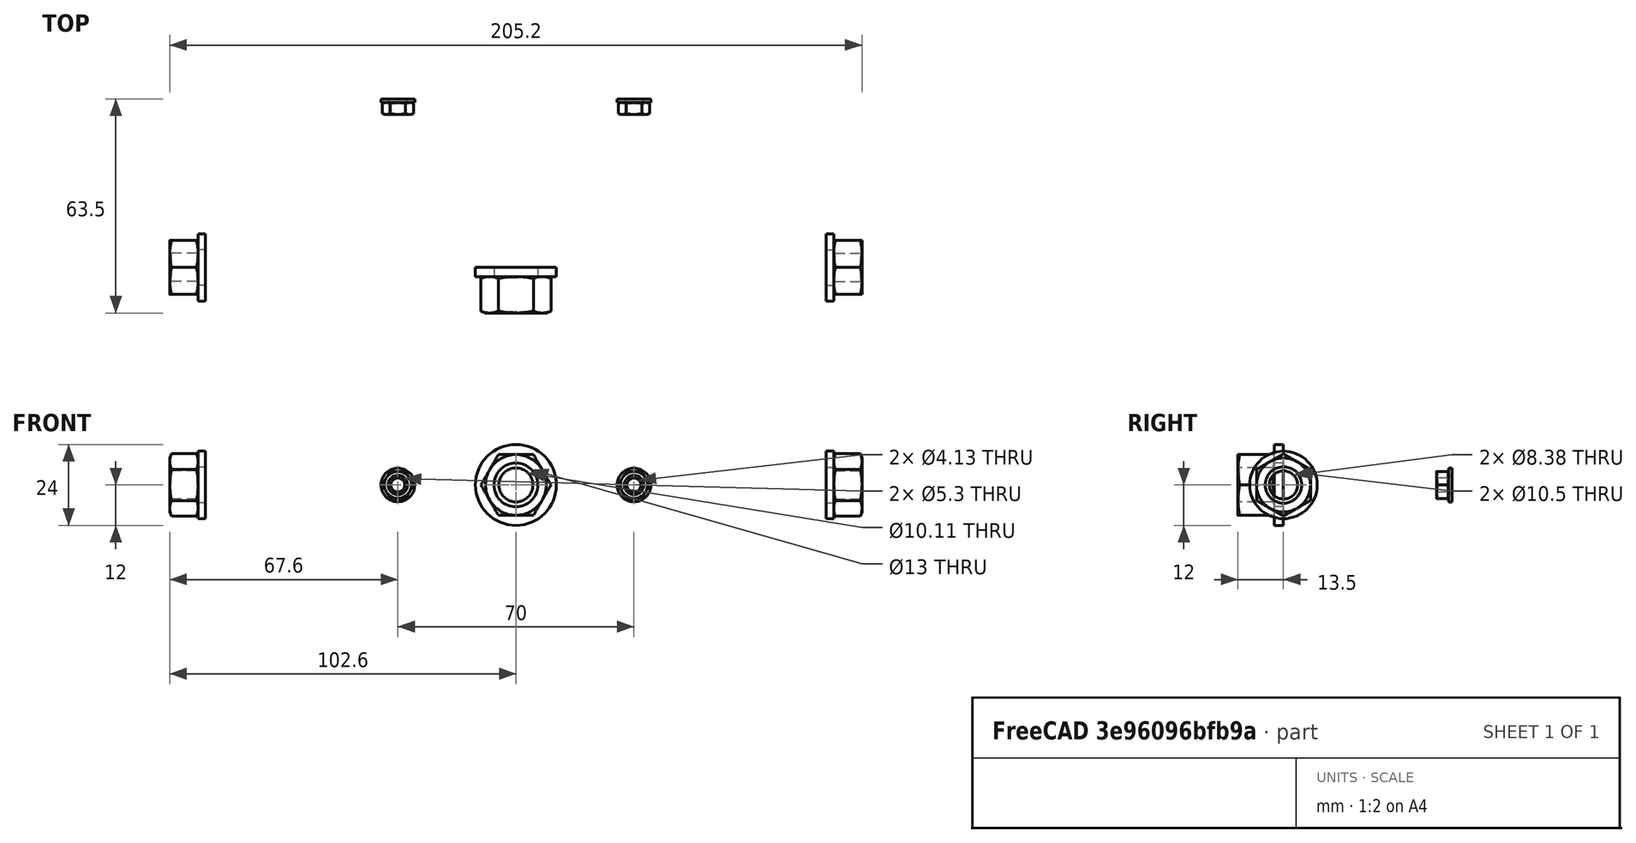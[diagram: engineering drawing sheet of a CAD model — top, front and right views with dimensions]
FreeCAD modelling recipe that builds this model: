
FCSTD DOCUMENT  (FreeCAD 0.19R)
Label: turnable_motor
License: All rights reserved
LicenseURL: http://en.wikipedia.org/wiki/All_rights_reserved
objects: Part::FeaturePython×10, PartDesign::CoordinateSystem×6, App::Link×6, App::DocumentObjectGroup×2, App::FeaturePython×1, App::Part×1
note: 16 computed .brp shape members not serialized (recipe doc carries the construction recipe); baked Part::Feature solids carry a one-line shape summary decoded from their .brp
EXTERNAL_REF file=frame.FCStd obj=LCS_1
EXTERNAL_REF file=frame.FCStd obj=Body
EXTERNAL_REF file=frame.FCStd obj=LCS_hole1
EXTERNAL_REF file=motor.FCStd obj=LCS_f1
EXTERNAL_REF file=motor.FCStd obj=Body
EXTERNAL_REF file=adapter.FCStd obj=LCS_1
EXTERNAL_REF file=motor.FCStd obj=shaft
EXTERNAL_REF file=adapter.FCStd obj=Body
EXTERNAL_REF file=adapter.FCStd obj=LCS_shaft_bottom
EXTERNAL_REF file=faceplate.FCStd obj=LCS_hole
EXTERNAL_REF file=faceplate.FCStd obj=Body
EXTERNAL_REF file=frame.FCStd obj=LCS_front1
EXTERNAL_REF file=frame.FCStd obj=LCS_front2
EXTERNAL_REF file=frame.FCStd obj=LCS_axis
EXTERNAL_REF file=stand.FCStd obj=LCS_hole
EXTERNAL_REF file=stand.FCStd obj=Body
EXTERNAL_REF file=stand.FCStd obj=LCS_sh2
EXTERNAL_REF file=stand.FCStd obj=LCS_sh1
EXTERNAL_REF file=disc.FCStd obj=LCS_back
EXTERNAL_REF file=faceplate.FCStd obj=LCS_front
EXTERNAL_REF file=disc.FCStd obj=Body
EXTERNAL_REF file=disc.FCStd obj=LCS_disc_front

FEATURE [App::DocumentObjectGroup] Parts
FEATURE [PartDesign::CoordinateSystem] LCS_Origin
  AttacherType = Attacher::AttachEngine3D
  MapMode = 2
  Support = -> [X_Axis]
FEATURE [App::DocumentObjectGroup] Constraints
FEATURE [App::FeaturePython] Variables  # WARN: FeaturePython — macro-defined, semantics opaque (R4)
FEATURE [App::Link] frame_Body
  AssemblyType = Asm4EE
  AttachedBy = #LCS_1
  AttachedTo = Parent Assembly#LCS_Origin
  AttachmentOffset = pos=(0,0,0) rot=(0.57735,0.57735,0.57735;2.0944rad)
  LinkPlacement = pos=(-56,1.51e-14,8e-15) rot=(0,0,1;0rad)
  LinkedObject = -> <external frame.FCStd>#Body
  Placement = pos=(-56,1.51e-14,8e-15) rot=(0,0,1;0rad)
  expr: Placement = LCS_Origin.Placement * AttachmentOffset * frame#LCS_1.Placement ^ -1
FEATURE [App::Link] motor_Body
  AssemblyType = Asm4EE
  AttachedBy = #LCS_f1
  AttachedTo = frame_Body#LCS_hole1
  LinkPlacement = pos=(-56,94,56) rot=(0,0,1;0rad)
  LinkedObject = -> <external motor.FCStd>#Body
  Placement = pos=(-56,94,56) rot=(0,0,1;0rad)
  expr: Placement = frame_Body.Placement * frame#LCS_hole1.Placement * AttachmentOffset * motor#LCS_f1.Placement ^ -1
FEATURE [App::Link] adapter_Body
  AssemblyType = Asm4EE
  AttachedBy = #LCS_1
  AttachedTo = motor_Body#shaft
  AttachmentOffset = pos=(0,0,0) rot=(1,0,0;3.14159rad)
  LinkPlacement = pos=(-56,-6,56) rot=(0,1,0;3.14159rad)
  LinkedObject = -> <external adapter.FCStd>#Body
  Placement = pos=(-56,-6,56) rot=(0,1,0;3.14159rad)
  expr: Placement = motor_Body.Placement * motor#shaft.Placement * AttachmentOffset * adapter#LCS_1.Placement ^ -1
FEATURE [App::Link] faceplate_Body
  AssemblyType = Asm4EE
  AttachedBy = #LCS_hole
  AttachedTo = adapter_Body#LCS_shaft_bottom
  AttachmentOffset = pos=(0,0,0) rot=(1,0,0;3.14159rad)
  LinkPlacement = pos=(-56,-39,56) rot=(0,0,1;0rad)
  LinkedObject = -> <external faceplate.FCStd>#Body
  Placement = pos=(-56,-39,56) rot=(0,0,1;0rad)
  expr: Placement = adapter_Body.Placement * adapter#LCS_shaft_bottom.Placement * AttachmentOffset * faceplate#LCS_hole.Placement ^ -1
FEATURE [Part::FeaturePython] Washer001  label="M5-Washer"  # Fasteners workbench fastener (typed FeaturePython)
  AssemblyType = Asm4EE
  AttachedBy = Origin
  AttachedTo = frame_Body#LCS_front1
  Placement = pos=(-91,3.92e-14,56) rot=(0.57735,-0.57735,0.57735;2.0944rad)
  diameter = 6
  invert = false
  matchOuter = false
  offset = 0
  type = 3
  expr: Placement = frame_Body.Placement * frame#LCS_front1.Placement * AttachmentOffset
FEATURE [Part::FeaturePython] Washer002  label="M5-Washer001"  # Fasteners workbench fastener (typed FeaturePython)
  AssemblyType = Asm4EE
  AttachedBy = Origin
  AttachedTo = frame_Body#LCS_front2
  Placement = pos=(-21,1.59e-14,56) rot=(0.57735,-0.57735,0.57735;2.0944rad)
  diameter = 6
  invert = false
  matchOuter = false
  offset = 0
  type = 3
  expr: Placement = frame_Body.Placement * frame#LCS_front2.Placement * AttachmentOffset
FEATURE [PartDesign::CoordinateSystem] LCS_w1
  AttacherType = Attacher::AttachEngine3D
  MapMode = 11
  Placement = pos=(-21,-1.1,56) rot=(0,-0.707107,0.707107;3.14159rad)
  Support = -> [Washer002]
FEATURE [PartDesign::CoordinateSystem] LCS_w2
  AttacherType = Attacher::AttachEngine3D
  MapMode = 11
  Placement = pos=(-91,-1.1,56) rot=(0,-0.707107,0.707107;3.14159rad)
  Support = -> [Washer001]
FEATURE [Part::FeaturePython] Nut001  label="M5-Nut"  # Fasteners workbench fastener (typed FeaturePython)
  AssemblyType = Asm4EE
  AttachedBy = Origin
  AttachedTo = Parent Assembly#LCS_w1
  Placement = pos=(-21,-1.1,56) rot=(0,-0.707107,0.707107;3.14159rad)
  diameter = 7
  invert = false
  matchOuter = false
  offset = 0
  thread = false
  type = 7
  expr: Placement = LCS_w1.Placement * AttachmentOffset
FEATURE [Part::FeaturePython] Nut002  label="M5-Nut001"  # Fasteners workbench fastener (typed FeaturePython)
  AssemblyType = Asm4EE
  AttachedBy = Origin
  AttachedTo = Parent Assembly#LCS_w2
  Placement = pos=(-91,-1.1,56) rot=(0,-0.707107,0.707107;3.14159rad)
  diameter = 7
  invert = false
  matchOuter = false
  offset = 0
  thread = false
  type = 7
  expr: Placement = LCS_w2.Placement * AttachmentOffset
FEATURE [App::Link] stand_Body
  AssemblyType = Asm4EE
  AttachedBy = #LCS_hole
  AttachedTo = frame_Body#LCS_axis
  AttachmentOffset = pos=(0,0,0) rot=(0.707107,-0.707107,0;3.14159rad)
  LinkPlacement = pos=(-56,-250,-180) rot=(0,0,-1;3.14159rad)
  LinkedObject = -> <external stand.FCStd>#Body
  Placement = pos=(-56,-250,-180) rot=(0,0,-1;3.14159rad)
  expr: Placement = frame_Body.Placement * frame#LCS_axis.Placement * AttachmentOffset * stand#LCS_hole.Placement ^ -1
FEATURE [Part::FeaturePython] Washer003  label="M10-Washer"  # Fasteners workbench fastener (typed FeaturePython)
  AssemblyType = Asm4EE
  AttachedBy = Origin
  AttachedTo = stand_Body#LCS_sh2
  AttachmentOffset = pos=(0,0,0) rot=(1,0,0;3.14159rad)
  Placement = pos=(36,-50,56) rot=(0.57735,0.57735,0.57735;2.0944rad)
  diameter = 9
  invert = false
  matchOuter = false
  offset = 0
  type = 3
  expr: Placement = stand_Body.Placement * stand#LCS_sh2.Placement * AttachmentOffset
FEATURE [PartDesign::CoordinateSystem] LCS_sw1
  AttacherType = Attacher::AttachEngine3D
  MapMode = 11
  Placement = pos=(38.2,-50,56) rot=(0.707107,0,0.707107;3.14159rad)
  Support = -> [Washer003]
FEATURE [Part::FeaturePython] Nut003  label="M10-Nut"  # Fasteners workbench fastener (typed FeaturePython)
  AssemblyType = Asm4EE
  AttachedBy = Origin
  AttachedTo = Parent Assembly#LCS_sw1
  Placement = pos=(38.2,-50,56) rot=(0.707107,0,0.707107;3.14159rad)
  diameter = 10
  invert = false
  matchOuter = false
  offset = 0
  thread = false
  type = 7
  expr: Placement = LCS_sw1.Placement * AttachmentOffset
FEATURE [Part::FeaturePython] Washer004  label="M10-Washer001"  # Fasteners workbench fastener (typed FeaturePython)
  AssemblyType = Asm4EE
  AttachedBy = Origin
  AttachedTo = stand_Body#LCS_sh1
  Placement = pos=(-148,-50,56) rot=(-0.57735,-0.57735,0.57735;2.0944rad)
  diameter = 9
  invert = false
  matchOuter = false
  offset = 0
  type = 3
  expr: Placement = stand_Body.Placement * stand#LCS_sh1.Placement * AttachmentOffset
FEATURE [PartDesign::CoordinateSystem] LCS_sw2
  AttacherType = Attacher::AttachEngine3D
  MapMode = 11
  Placement = pos=(-150.2,-50,56) rot=(-0.707107,0,0.707107;3.14159rad)
  Support = -> [Washer004]
FEATURE [Part::FeaturePython] Nut005  label="M10-Nut001"  # Fasteners workbench fastener (typed FeaturePython)
  AssemblyType = Asm4EE
  AttachedBy = Origin
  AttachedTo = Parent Assembly#LCS_sw2
  Placement = pos=(-150.2,-50,56) rot=(-0.707107,0,0.707107;3.14159rad)
  diameter = 10
  invert = false
  matchOuter = false
  offset = 0
  thread = false
  type = 7
  expr: Placement = LCS_sw2.Placement * AttachmentOffset
FEATURE [App::Link] disc_Body
  AssemblyType = Asm4EE
  AttachedBy = #LCS_back
  AttachedTo = faceplate_Body#LCS_front
  AttachmentOffset = pos=(0,0,0) rot=(1,0,0;3.14159rad)
  LinkPlacement = pos=(-56,-49,56) rot=(0,1,0;3.14159rad)
  LinkedObject = -> <external disc.FCStd>#Body
  Placement = pos=(-56,-49,56) rot=(0,1,0;3.14159rad)
  expr: Placement = faceplate_Body.Placement * faceplate#LCS_front.Placement * AttachmentOffset * disc#LCS_back.Placement ^ -1
FEATURE [Part::FeaturePython] Washer  label="M12-Washer"  # Fasteners workbench fastener (typed FeaturePython)
  AssemblyType = Asm4EE
  AttachedBy = Origin
  AttachedTo = disc_Body#LCS_disc_front
  Placement = pos=(-56,-50,56) rot=(0.57735,0.57735,-0.57735;2.0944rad)
  diameter = 10
  invert = false
  matchOuter = false
  offset = 0
  type = 3
  expr: Placement = disc_Body.Placement * disc#LCS_disc_front.Placement * AttachmentOffset
FEATURE [PartDesign::CoordinateSystem] LCS_1
  AttacherType = Attacher::AttachEngine3D
  MapMode = 11
  Placement = pos=(-56,-52.7,56) rot=(1,0,0;1.5708rad)
  Support = -> [Washer]
FEATURE [Part::FeaturePython] Nut  label="M12-Nut"  # Fasteners workbench fastener (typed FeaturePython)
  AssemblyType = Asm4EE
  AttachedBy = Origin
  AttachedTo = Parent Assembly#LCS_1
  Placement = pos=(-56,-52.7,56) rot=(1,0,0;1.5708rad)
  diameter = 11
  invert = false
  matchOuter = false
  offset = 0
  thread = false
  type = 7
  expr: Placement = LCS_1.Placement * AttachmentOffset
FEATURE [App::Part] Model
  Configuration = 0
  Group = -> [LCS_Origin,Constraints,Variables,frame_Body,motor_Body,adapter_Body,faceplate_Body,Washer001,Washer002,LCS_w1,LCS_w2,Nut001,Nut002,stand_Body,Washer003,LCS_sw1,Nut003,Washer004,LCS_sw2,Nut005,disc_Body,Washer,LCS_1,Nut]
  Origin = -> Origin
  Type = Assembly4 Model

RESOLVED EXTERNAL PARTS (link-assembly join: the EXTERNAL_REF files above that resolve inside this repo's crawl, each included once):
---- part adapter.FCStd = doc fcstd_3b703603a306 ----
FCSTD DOCUMENT  (FreeCAD 0.19R)
Label: adapter
License: All rights reserved
LicenseURL: http://en.wikipedia.org/wiki/All_rights_reserved
objects: Sketcher::SketchObject×3, PartDesign::Pad×2, PartDesign::CoordinateSystem×2, PartDesign::Pocket×1, PartDesign::Body×1
note: 12 computed .brp shape members not serialized (recipe doc carries the construction recipe); baked Part::Feature solids carry a one-line shape summary decoded from their .brp

FEATURE [Sketcher::SketchObject] Sketch
  FullyConstrained = false
  MapMode = 5
  Placement = pos=(0,0,0) rot=(1,0,0;1.5708rad)
  Support = -> [XZ_Plane]
  sketch-geometry (1):
    g0: Circle CenterX=0 CenterY=0 CenterZ=0 NormalX=0 NormalY=0 NormalZ=1 AngleXU=0 Radius=9.5
  constraints (1):
    c: Diameter(g0) = 19
FEATURE [PartDesign::Pad] Pad
  Direction = (1,1,1)
  Length = 33
  Length2 = 100
  Placement = pos=(0,0,0) rot=(1,0,0;1.5708rad)
  Profile = -> Sketch
  Type = 0
FEATURE [Sketcher::SketchObject] Sketch001
  FullyConstrained = true
  MapMode = 5
  Placement = pos=(0,0,0) rot=(-1,0,0;1.5708rad)
  Support = -> [Pad]
  sketch-geometry (1):
    g0: Circle CenterX=0 CenterY=0 CenterZ=0 NormalX=0 NormalY=0 NormalZ=1 AngleXU=0 Radius=4
  constraints (2):
    c: Coincident(g0,g-1)
    c: Diameter(g0) = 8
FEATURE [PartDesign::Pocket] Pocket
  BaseFeature = -> Pad
  Length = 30
  Length2 = 100
  Placement = pos=(0,0,0) rot=(1,0,0;1.5708rad)
  Profile = -> Sketch001
  Type = 0
FEATURE [Sketcher::SketchObject] Sketch002
  FullyConstrained = true
  MapMode = 5
  Placement = pos=(0,-33,7.3e-15) rot=(1,0,0;1.5708rad)
  Support = -> [Pocket]
  sketch-geometry (1):
    g0: Circle CenterX=0 CenterY=0 CenterZ=0 NormalX=0 NormalY=0 NormalZ=1 AngleXU=0 Radius=6.25
  constraints (2):
    c: Coincident(g0,g-1)
    c: Diameter(g0) = 12.5
FEATURE [PartDesign::Pad] Pad001
  BaseFeature = -> Pocket
  Direction = (1,1,1)
  Length = 23.5
  Length2 = 100
  Placement = pos=(0,0,0) rot=(1,0,0;1.5708rad)
  Profile = -> Sketch002
  Type = 0
FEATURE [PartDesign::CoordinateSystem] LCS_1
  AttacherType = Attacher::AttachEngine3D
  MapMode = 11
  Placement = pos=(0,-30,2.8e-14) rot=(0.57735,-0.57735,-0.57735;4.18879rad)
  Support = -> [Pad001]
FEATURE [PartDesign::CoordinateSystem] LCS_shaft_bottom
  AttacherType = Attacher::AttachEngine3D
  MapMode = 11
  Placement = pos=(0,-33,3.7e-14) rot=(0.57735,-0.57735,0.57735;2.0944rad)
  Support = -> [Pad001]
FEATURE [PartDesign::Body] Body
  Group = -> [Sketch,Pad,Sketch001,Pocket,Sketch002,Pad001,LCS_1,LCS_shaft_bottom]
  Origin = -> Origin
  Tip = -> Pad001
---- part disc.FCStd = doc fcstd_dda78c2396a7 ----
FCSTD DOCUMENT  (FreeCAD 0.19R)
Label: disc
License: All rights reserved
LicenseURL: http://en.wikipedia.org/wiki/All_rights_reserved
objects: TechDraw::DrawViewDimension×4, TechDraw::DrawViewPart×3, PartDesign::CoordinateSystem×2, Sketcher::SketchObject×1, PartDesign::Pad×1, PartDesign::Body×1, TechDraw::DrawSVGTemplate×1, TechDraw::DrawPage×1
note: 6 computed .brp shape members not serialized (recipe doc carries the construction recipe); baked Part::Feature solids carry a one-line shape summary decoded from their .brp

FEATURE [Sketcher::SketchObject] Sketch
  FullyConstrained = true
  MapMode = 5
  Placement = pos=(0,0,0) rot=(1,0,0;1.5708rad)
  Support = -> [XZ_Plane]
  sketch-geometry (2):
    g0: Circle CenterX=0 CenterY=0 CenterZ=0 NormalX=0 NormalY=0 NormalZ=1 AngleXU=0 Radius=77
    g1: Circle CenterX=0 CenterY=0 CenterZ=0 NormalX=0 NormalY=0 NormalZ=1 AngleXU=0 Radius=6.35
  constraints (4):
    c: Coincident(g0,g-1)
    c: Coincident(g1,g0)
    c: Diameter(g1) = 12.7
    c: Diameter(g0) = 154
FEATURE [PartDesign::Pad] Pad
  Direction = (1,1,1)
  Length = 1
  Length2 = 100
  Placement = pos=(0,0,0) rot=(1,0,0;1.5708rad)
  Profile = -> Sketch
  Type = 0
FEATURE [PartDesign::CoordinateSystem] LCS_back
  AttacherType = Attacher::AttachEngine3D
  MapMode = 11
  Placement = pos=(0,0,0) rot=(0.57735,-0.57735,0.57735;2.0944rad)
  Support = -> [Pad]
FEATURE [PartDesign::CoordinateSystem] LCS_disc_front
  AttacherType = Attacher::AttachEngine3D
  MapMode = 11
  Placement = pos=(0,-1,0) rot=(0.57735,-0.57735,0.57735;2.0944rad)
  Support = -> [Pad]
FEATURE [PartDesign::Body] Body
  Group = -> [Sketch,Pad,LCS_back,LCS_disc_front]
  Origin = -> Origin
  Tip = -> Pad
FEATURE [TechDraw::DrawSVGTemplate] Template
  EditableTexts = Designed_by_Name=Designed by Name; Drawing_number=Drawing number; FC-Date=Date; FC-SC=Scale; FC-SH=Sheet; FC-Title=Title; Subtitle=Subtitle; Weight=Weight
  Height = 210
  Orientation = 1
  Width = 297
FEATURE [TechDraw::DrawViewPart] View
  CoarseView = false
  Direction = (0,-1,0)
  Focus = 100
  HardHidden = false
  IsoCount = 0
  IsoHidden = false
  IsoVisible = false
  LockPosition = false
  Perspective = false
  Rotation = 0
  Scale = 0.3
  ScaleType = 0
  SeamHidden = false
  SeamVisible = true
  SmoothHidden = false
  SmoothVisible = true
  Source = -> [Pad]
  X = 80.5
  XDirection = (-0.494,0,-0.83)
  Y = 155
FEATURE [TechDraw::DrawViewPart] View001
  CoarseView = false
  Direction = (0.264,-0.596,0.758)
  Focus = 100
  HardHidden = false
  IsoCount = 0
  IsoHidden = false
  IsoVisible = false
  LockPosition = false
  Perspective = false
  Rotation = 0
  Scale = 0.4
  ScaleType = 0
  SeamHidden = false
  SeamVisible = true
  SmoothHidden = false
  SmoothVisible = true
  Source = -> [Body]
  X = 215.5
  XDirection = (0.492,0.759,0.426)
  Y = 152
FEATURE [TechDraw::DrawViewPart] View002
  CoarseView = false
  Direction = (0,0,1)
  Focus = 100
  HardHidden = false
  IsoCount = 0
  IsoHidden = false
  IsoVisible = false
  LockPosition = false
  Perspective = false
  Rotation = 0
  Scale = 0.7
  ScaleType = 0
  SeamHidden = false
  SeamVisible = true
  SmoothHidden = false
  SmoothVisible = true
  Source = -> [Body]
  X = 90.5
  XDirection = (1,0,0)
  Y = 87
FEATURE [TechDraw::DrawViewDimension] Dimension
  Arbitrary = false
  ArbitraryTolerances = false
  EqualTolerance = true
  FormatSpec = %.2f
  FormatSpecOverTolerance = %+.2f
  FormatSpecUnderTolerance = %+.2f
  Inverted = false
  LockPosition = false
  MeasureType = 1
  OverTolerance = 0
  References2D = -> [View002]
  Rotation = 0
  ScaleType = 0
  TheoreticalExact = false
  Type = 0
  UnderTolerance = 0
  X = 0
  Y = -0.5
FEATURE [TechDraw::DrawViewDimension] Dimension002
  Arbitrary = false
  ArbitraryTolerances = false
  EqualTolerance = true
  FormatSpec = ⌀%.2f
  FormatSpecOverTolerance = %+.2f
  FormatSpecUnderTolerance = %+.2f
  Inverted = false
  LockPosition = false
  MeasureType = 1
  OverTolerance = 0
  References2D = -> [View]
  Rotation = 0
  ScaleType = 0
  TheoreticalExact = false
  Type = 5
  UnderTolerance = 0
  X = -13
  Y = 0
FEATURE [TechDraw::DrawViewDimension] Dimension004
  Arbitrary = false
  ArbitraryTolerances = false
  EqualTolerance = true
  FormatSpec = %.2f
  FormatSpecOverTolerance = %+.2f
  FormatSpecUnderTolerance = %+.2f
  Inverted = false
  LockPosition = false
  MeasureType = 1
  OverTolerance = 0
  References2D = -> [View002]
  Rotation = 0
  ScaleType = 0
  TheoreticalExact = false
  Type = 2
  UnderTolerance = 0
  X = 61.9
  Y = 0
FEATURE [TechDraw::DrawViewDimension] Dimension005
  Arbitrary = false
  ArbitraryTolerances = false
  EqualTolerance = true
  FormatSpec = ⌀%.2f
  FormatSpecOverTolerance = %+.2f
  FormatSpecUnderTolerance = %+.2f
  Inverted = false
  LockPosition = false
  MeasureType = 1
  OverTolerance = 0
  References2D = -> [View]
  Rotation = 0
  ScaleType = 0
  TheoreticalExact = false
  Type = 5
  UnderTolerance = 0
  X = 12
  Y = 0
FEATURE [TechDraw::DrawPage] Page
  KeepUpdated = true
  NextBalloonIndex = 1
  ProjectionType = 0
  Template = -> Template
  Views = -> [View,View001,View002,Dimension,Dimension002,Dimension004,Dimension005]
---- part faceplate.FCStd = doc fcstd_74a67d757d3e ----
FCSTD DOCUMENT  (FreeCAD 0.19R)
Label: faceplate
License: All rights reserved
LicenseURL: http://en.wikipedia.org/wiki/All_rights_reserved
objects: Sketcher::SketchObject×3, PartDesign::Pocket×2, PartDesign::CoordinateSystem×2, PartDesign::Pad×1, PartDesign::Body×1
note: 12 computed .brp shape members not serialized (recipe doc carries the construction recipe); baked Part::Feature solids carry a one-line shape summary decoded from their .brp

FEATURE [Sketcher::SketchObject] Sketch
  FullyConstrained = true
  MapMode = 5
  Placement = pos=(0,0,0) rot=(1,0,0;1.5708rad)
  Support = -> [XZ_Plane]
  sketch-geometry (1):
    g0: Circle CenterX=0 CenterY=0 CenterZ=0 NormalX=0 NormalY=0 NormalZ=1 AngleXU=0 Radius=74.5
  constraints (2):
    c: Coincident(g0,g-1)
    c: Diameter(g0) = 149
FEATURE [PartDesign::Pad] Pad
  Direction = (1,1,1)
  Length = 10
  Length2 = 100
  Placement = pos=(0,0,0) rot=(1,0,0;1.5708rad)
  Profile = -> Sketch
  Type = 0
FEATURE [Sketcher::SketchObject] Sketch001
  FullyConstrained = true
  MapMode = 5
  Placement = pos=(0,0,0) rot=(-1,0,0;1.5708rad)
  Support = -> [Pad]
  sketch-geometry (1):
    g0: Circle CenterX=0 CenterY=0 CenterZ=0 NormalX=0 NormalY=0 NormalZ=1 AngleXU=0 Radius=6.35
  constraints (2):
    c: Coincident(g0,g-1)
    c: Diameter(g0) = 12.7
FEATURE [PartDesign::Pocket] Pocket
  BaseFeature = -> Pad
  Length = 5
  Length2 = 100
  Placement = pos=(0,0,0) rot=(1,0,0;1.5708rad)
  Profile = -> Sketch001
  Type = 1
FEATURE [PartDesign::CoordinateSystem] LCS_hole
  AttacherType = Attacher::AttachEngine3D
  MapMode = 11
  Placement = pos=(0,0,0) rot=(0.57735,-0.57735,-0.57735;4.18879rad)
  Support = -> [Pocket]
FEATURE [Sketcher::SketchObject] Sketch002
  FullyConstrained = true
  MapMode = 5
  Placement = pos=(0,0,0) rot=(-1,0,0;1.5708rad)
  Support = -> [Pocket]
  sketch-geometry (2):
    g0: Circle CenterX=0 CenterY=0 CenterZ=0 NormalX=0 NormalY=0 NormalZ=1 AngleXU=0 Radius=65
    g1: Circle CenterX=0 CenterY=0 CenterZ=0 NormalX=0 NormalY=0 NormalZ=1 AngleXU=0 Radius=34.5
  constraints (4):
    c: Coincident(g0,g-1)
    c: Coincident(g1,g0)
    c: Diameter(g1) = 69
    c: Diameter(g0) = 130
FEATURE [PartDesign::Pocket] Pocket001
  BaseFeature = -> Pocket
  Length = 6
  Length2 = 100
  Placement = pos=(0,0,0) rot=(1,0,0;1.5708rad)
  Profile = -> Sketch002
  Type = 0
FEATURE [PartDesign::CoordinateSystem] LCS_front
  AttacherType = Attacher::AttachEngine3D
  MapMode = 11
  Placement = pos=(0,-10,8.9e-15) rot=(0.57735,-0.57735,-0.57735;4.18879rad)
  Support = -> [Pocket001]
FEATURE [PartDesign::Body] Body
  Group = -> [Sketch,Pad,Sketch001,Pocket,LCS_hole,Sketch002,Pocket001,LCS_front]
  Origin = -> Origin
  Tip = -> Pocket001
---- part frame.FCStd = doc fcstd_d6c5ef4f96c6 ----
FCSTD DOCUMENT  (FreeCAD 0.19R)
Label: frame
License: All rights reserved
LicenseURL: http://en.wikipedia.org/wiki/All_rights_reserved
objects: Sketcher::SketchObject×10, PartDesign::Pad×6, PartDesign::CoordinateSystem×6, PartDesign::Pocket×4, PartDesign::Body×1
note: 37 computed .brp shape members not serialized (recipe doc carries the construction recipe); baked Part::Feature solids carry a one-line shape summary decoded from their .brp

FEATURE [Sketcher::SketchObject] Sketch
  FullyConstrained = true
  MapMode = 5
  Support = -> [XY_Plane]
  sketch-geometry (8):
    g0: LineSegment StartX=-56 StartY=32 StartZ=0 EndX=-56 EndY=0 EndZ=0
    g1: LineSegment StartX=56 StartY=32 StartZ=0 EndX=56 EndY=0 EndZ=0
    g2: LineSegment StartX=56 StartY=0 StartZ=0 EndX=-56 EndY=0 EndZ=0
    g3: LineSegment StartX=52 StartY=28 StartZ=0 EndX=52 EndY=4 EndZ=0
    g4: LineSegment StartX=52 StartY=4 StartZ=0 EndX=-52 EndY=4 EndZ=0
    g5: LineSegment StartX=-52 StartY=4 StartZ=0 EndX=-52 EndY=28 EndZ=0
    g6: ArcOfCircle CenterX=-56 CenterY=28 CenterZ=0 NormalX=0 NormalY=0 NormalZ=1 AngleXU=0 Radius=4 StartAngle=-3.64e-14 EndAngle=1.5708
    g7: ArcOfCircle CenterX=56 CenterY=28 CenterZ=0 NormalX=0 NormalY=0 NormalZ=1 AngleXU=0 Radius=4 StartAngle=1.5708 EndAngle=3.14159
  constraints (24):
    c: PointOnObject(g0,g-1)
    c: Vertical(g0)
    c: PointOnObject(g1,g-1)
    c: Vertical(g1)
    c: Coincident(g2,g1)
    c: Vertical(g3)
    c: Coincident(g4,g3)
    c: Horizontal(g4)
    c: Vertical(g5)
    c: DistanceX(g0,g1) = 112
    c: Symmetric(g0,g1,g-2)
    c: DistanceX(g3,g1) = 4
    c: DistanceY(g2,g4) = 4
    c: Symmetric(g5,g3,g-2)
    c: Coincident(g4,g5)
    c: Coincident(g2,g0)
    c: DistanceY(g4,g5) = 24
    c: DistanceY(g0,g0) = 32
    c: PointOnObject(g6,g0)
    c: Coincident(g6,g5)
    c: Coincident(g6,g0)
    c: PointOnObject(g7,g1)
    c: Coincident(g7,g3)
    c: Coincident(g7,g1)
FEATURE [PartDesign::Pad] Pad
  Direction = (1,1,1)
  Length = 112
  Length2 = 100
  Profile = -> Sketch
  Type = 0
FEATURE [Sketcher::SketchObject] Sketch001
  FullyConstrained = true
  MapMode = 5
  Placement = pos=(56,0,0) rot=(0.57735,0.57735,0.57735;2.0944rad)
  Support = -> [Pad]
  sketch-geometry (8):
    g0: LineSegment StartX=0 StartY=112 StartZ=0 EndX=32 EndY=112 EndZ=0
    g1: LineSegment StartX=0 StartY=108 StartZ=0 EndX=28 EndY=108 EndZ=0
    g2: LineSegment StartX=0 StartY=108 StartZ=0 EndX=0 EndY=112 EndZ=0
    g3: ArcOfCircle CenterX=28 CenterY=112 CenterZ=0 NormalX=0 NormalY=0 NormalZ=1 AngleXU=0 Radius=4 StartAngle=4.71239 EndAngle=6.28319
    g4: LineSegment StartX=0 StartY=0 StartZ=0 EndX=32 EndY=0 EndZ=0
    g5: LineSegment StartX=0 StartY=0 StartZ=0 EndX=0 EndY=4 EndZ=0
    g6: LineSegment StartX=0 StartY=4 StartZ=0 EndX=28 EndY=4 EndZ=0
    g7: ArcOfCircle CenterX=28 CenterY=0 CenterZ=0 NormalX=0 NormalY=0 NormalZ=1 AngleXU=0 Radius=4 StartAngle=0 EndAngle=1.5708
  constraints (25):
    c: PointOnObject(g0,g-2)
    c: Horizontal(g0)
    c: PointOnObject(g1,g-2)
    c: Horizontal(g1)
    c: Coincident(g2,g1)
    c: Coincident(g2,g0)
    c: DistanceX(g0,g0) = 32
    c: DistanceX(g1,g1) = 28
    c: DistanceY(g1,g0) = 4
    c: DistanceY(g-1,g0) = 112
    c: PointOnObject(g3,g0)
    c: Coincident(g3,g0)
    c: Coincident(g3,g1)
    c: Coincident(g4,g-1)
    c: PointOnObject(g4,g-1)
    c: DistanceX(g4,g4) = 32
    c: Coincident(g5,g4)
    c: PointOnObject(g5,g-2)
    c: Coincident(g6,g5)
    c: Horizontal(g6)
    c: DistanceY(g4,g5) = 4
    c: DistanceX(g5,g6) = 28
    c: PointOnObject(g7,g4)
    c: Coincident(g7,g6)
    c: Coincident(g7,g4)
FEATURE [PartDesign::Pad] Pad001
  BaseFeature = -> Pad
  Direction = (1,1,1)
  Length = 112
  Length2 = 100
  Profile = -> Sketch001
  Reversed = true
  Type = 0
FEATURE [Sketcher::SketchObject] Sketch002
  ExternalGeometry = -> [Pad001]
  FullyConstrained = true
  MapMode = 5
  Placement = pos=(0,0,0) rot=(1,0,0;1.5708rad)
  Support = -> [Pad001]
  sketch-geometry (6):
    g0: LineSegment StartX=-24 StartY=80 StartZ=0 EndX=24 EndY=80 EndZ=0
    g1: LineSegment StartX=24 StartY=80 StartZ=0 EndX=24 EndY=32 EndZ=0
    g2: LineSegment StartX=24 StartY=32 StartZ=0 EndX=-24 EndY=32 EndZ=0
    g3: LineSegment StartX=-24 StartY=32 StartZ=0 EndX=-24 EndY=80 EndZ=0
    g4: Circle CenterX=-35 CenterY=56 CenterZ=0 NormalX=0 NormalY=0 NormalZ=1 AngleXU=0 Radius=2.75
    g5: Circle CenterX=35 CenterY=56 CenterZ=0 NormalX=0 NormalY=0 NormalZ=1 AngleXU=0 Radius=2.75
  constraints (16):
    c: Coincident(g0,g1)
    c: Coincident(g1,g2)
    c: Coincident(g2,g3)
    c: Coincident(g3,g0)
    c: Horizontal(g0)
    c: Vertical(g1)
    c: Vertical(g3)
    c: DistanceX(g1,g-4) = 32
    c: DistanceY(g-4,g2) = 32
    c: Symmetric(g2,g1,g-2)
    c: Equal(g2,g3)
    c: Equal(g5,g4)
    c: Diameter(g5) = 5.5
    c: Symmetric(g5,g4,g-2)
    c: DistanceX(g4,g5) = 70
    c: DistanceY(g-4,g4) = 56
FEATURE [PartDesign::Pocket] Pocket
  BaseFeature = -> Pad001
  Length = 5
  Length2 = 100
  Profile = -> Sketch002
  Type = 1
FEATURE [PartDesign::CoordinateSystem] LCS_hole1
  AttacherType = Attacher::AttachEngine3D
  MapMode = 11
  Placement = pos=(-35,4,56) rot=(0.57735,-0.57735,0.57735;2.0944rad)
  Support = -> [Pocket]
FEATURE [PartDesign::CoordinateSystem] LCS_hole2
  AttacherType = Attacher::AttachEngine3D
  MapMode = 11
  Placement = pos=(35,4,56) rot=(0.57735,-0.57735,0.57735;2.0944rad)
  Support = -> [Pocket]
FEATURE [PartDesign::CoordinateSystem] LCS_1
  AttacherType = Attacher::AttachEngine3D
  MapMode = 7
  Placement = pos=(56,0,0) rot=(0.57735,0.57735,0.57735;2.0944rad)
  Support = -> [Pocket]
FEATURE [PartDesign::CoordinateSystem] LCS_front1
  AttacherType = Attacher::AttachEngine3D
  MapMode = 11
  Placement = pos=(-35,0,56) rot=(0.57735,-0.57735,0.57735;2.0944rad)
  Support = -> [Pocket]
FEATURE [PartDesign::CoordinateSystem] LCS_front2
  AttacherType = Attacher::AttachEngine3D
  MapMode = 11
  Placement = pos=(35,0,56) rot=(0.57735,-0.57735,0.57735;2.0944rad)
  Support = -> [Pocket]
FEATURE [Sketcher::SketchObject] Sketch003
  ExternalGeometry = -> [Pocket]
  FullyConstrained = true
  MapMode = 5
  Placement = pos=(0,0,0) rot=(1,0,0;1.5708rad)
  Support = -> [Pocket]
  sketch-geometry (12):
    g0: LineSegment StartX=56 StartY=72 StartZ=0 EndX=56 EndY=68 EndZ=0
    g1: LineSegment StartX=-56 StartY=72 StartZ=0 EndX=-56 EndY=68 EndZ=0
    g2: LineSegment StartX=-56 StartY=72 StartZ=0 EndX=-88 EndY=72 EndZ=0
    g3: LineSegment StartX=-88 StartY=72 StartZ=0 EndX=-88 EndY=40 EndZ=0
    g4: LineSegment StartX=56 StartY=72 StartZ=0 EndX=88 EndY=72 EndZ=0
    g5: LineSegment StartX=88 StartY=72 StartZ=0 EndX=88 EndY=40 EndZ=0
    g6: LineSegment StartX=56 StartY=68 StartZ=0 EndX=84 EndY=68 EndZ=0
    g7: LineSegment StartX=84 StartY=68 StartZ=0 EndX=84 EndY=44 EndZ=0
    g8: LineSegment StartX=-56 StartY=68 StartZ=0 EndX=-84 EndY=68 EndZ=0
    g9: LineSegment StartX=-84 StartY=68 StartZ=0 EndX=-84 EndY=44 EndZ=0
    g10: ArcOfCircle CenterX=-88 CenterY=44 CenterZ=0 NormalX=0 NormalY=0 NormalZ=1 AngleXU=0 Radius=4 StartAngle=4.71239 EndAngle=6.28319
    g11: ArcOfCircle CenterX=88 CenterY=44 CenterZ=0 NormalX=0 NormalY=0 NormalZ=1 AngleXU=0 Radius=4 StartAngle=3.14159 EndAngle=4.71239
  constraints (37):
    c: PointOnObject(g0,g-3)
    c: PointOnObject(g0,g-3)
    c: PointOnObject(g1,g-4)
    c: Coincident(g2,g1)
    c: Horizontal(g2)
    c: Coincident(g3,g2)
    c: Vertical(g3)
    c: Coincident(g4,g0)
    c: Horizontal(g4)
    c: Coincident(g5,g4)
    c: Vertical(g5)
    c: Horizontal(g6)
    c: Coincident(g7,g6)
    c: Vertical(g7)
    c: Coincident(g8,g1)
    c: Horizontal(g8)
    c: Coincident(g9,g8)
    c: Vertical(g9)
    c: Coincident(g0,g6)
    c: Equal(g0,g1)
    c: DistanceY(g1,g1) = 4
    c: DistanceX(g7,g5) = 4
    c: Equal(g4,g5)
    c: Equal(g5,g2)
    c: Equal(g2,g3)
    c: DistanceY(g3,g2) = 32
    c: DistanceX(g3,g9) = 4
    c: DistanceY(g9,g8) = 24
    c: DistanceY(g1,g-5) = 40
    c: Symmetric(g1,g0,g-2)
    c: Equal(g9,g7)
    c: PointOnObject(g10,g3)
    c: Coincident(g10,g9)
    c: Coincident(g10,g3)
    c: PointOnObject(g11,g5)
    c: Coincident(g11,g5)
    c: Coincident(g11,g7)
FEATURE [PartDesign::Pad] Pad002
  BaseFeature = -> Pocket
  Direction = (1,1,1)
  Length = 66
  Length2 = 150
  Profile = -> Sketch003
  Type = 4
FEATURE [Sketcher::SketchObject] Sketch004
  ExternalGeometry = -> [Pad002]
  FullyConstrained = true
  MapMode = 5
  Placement = pos=(0,1.58e-14,72) rot=(0,0,1;0rad)
  Support = -> [Pad002]
  sketch-geometry (8):
    g0: LineSegment StartX=56 StartY=-66 StartZ=0 EndX=84 EndY=-66 EndZ=0
    g1: LineSegment StartX=84 StartY=-66 StartZ=0 EndX=84 EndY=-33 EndZ=0
    g2: LineSegment StartX=84 StartY=-33 StartZ=0 EndX=56 EndY=-33 EndZ=0
    g3: LineSegment StartX=56 StartY=-33 StartZ=0 EndX=56 EndY=-66 EndZ=0
    g4: LineSegment StartX=-84 StartY=-66 StartZ=0 EndX=-56 EndY=-66 EndZ=0
    g5: LineSegment StartX=-56 StartY=-66 StartZ=0 EndX=-56 EndY=-33 EndZ=0
    g6: LineSegment StartX=-56 StartY=-33 StartZ=0 EndX=-84 EndY=-33 EndZ=0
    g7: LineSegment StartX=-84 StartY=-33 StartZ=0 EndX=-84 EndY=-66 EndZ=0
  constraints (22):
    c: Coincident(g0,g1)
    c: Coincident(g1,g2)
    c: Coincident(g2,g3)
    c: Coincident(g3,g0)
    c: Horizontal(g0)
    c: Horizontal(g2)
    c: Vertical(g1)
    c: Vertical(g3)
    c: Coincident(g0,g-4)
    c: DistanceX(g2,g1) = 28
    c: DistanceY(g0,g2) = 33
    c: Coincident(g4,g5)
    c: Coincident(g5,g6)
    c: Coincident(g6,g7)
    c: Coincident(g7,g4)
    c: Horizontal(g4)
    c: Horizontal(g6)
    c: Vertical(g5)
    c: Vertical(g7)
    c: Equal(g3,g7)
    c: Equal(g6,g2)
    c: Coincident(g4,g-3)
FEATURE [PartDesign::Pocket] Pocket001
  BaseFeature = -> Pad002
  Length = 5
  Length2 = 100
  Profile = -> Sketch004
  Type = 1
FEATURE [Sketcher::SketchObject] Sketch005
  ExternalGeometry = -> [Pocket001]
  FullyConstrained = true
  MapMode = 5
  Placement = pos=(88,0,0) rot=(0.57735,0.57735,0.57735;2.0944rad)
  Support = -> [Pocket001]
  sketch-geometry (3):
    g0: LineSegment StartX=-66 StartY=72 StartZ=0 EndX=-50 EndY=72 EndZ=0
    g1: LineSegment StartX=-66 StartY=72 StartZ=0 EndX=-66 EndY=56 EndZ=0
    g2: ArcOfCircle CenterX=-50 CenterY=56 CenterZ=0 NormalX=0 NormalY=0 NormalZ=1 AngleXU=0 Radius=16 StartAngle=1.5708 EndAngle=3.14159
  constraints (9):
    c: Horizontal(g0)
    c: DistanceX(g-3,g0) = 16
    c: PointOnObject(g1,g-3)
    c: Equal(g0,g1)
    c: DistanceY(g2,g0) = 16
    c: Coincident(g2,g0)
    c: Coincident(g2,g1)
    c: Coincident(g-3,g1)
    c: Coincident(g0,g1)
FEATURE [PartDesign::Pocket] Pocket002
  BaseFeature = -> Pocket001
  Length = 5
  Length2 = 100
  Profile = -> Sketch005
  Type = 1
FEATURE [Sketcher::SketchObject] Sketch006
  ExternalGeometry = -> [Pocket002]
  FullyConstrained = true
  MapMode = 5
  Placement = pos=(88,0,0) rot=(0.57735,0.57735,0.57735;2.0944rad)
  Support = -> [Pocket002]
  sketch-geometry (3):
    g0: LineSegment StartX=-50 StartY=40 StartZ=0 EndX=-66 EndY=40 EndZ=0
    g1: LineSegment StartX=-66 StartY=40 StartZ=0 EndX=-66 EndY=56 EndZ=0
    g2: ArcOfCircle CenterX=-50 CenterY=56 CenterZ=0 NormalX=0 NormalY=0 NormalZ=1 AngleXU=0 Radius=16 StartAngle=3.14159 EndAngle=4.71239
  constraints (9):
    c: PointOnObject(g0,g-3)
    c: Coincident(g0,g-3)
    c: Coincident(g1,g0)
    c: Vertical(g1)
    c: Coincident(g2,g0)
    c: Coincident(g2,g1)
    c: Equal(g0,g1)
    c: DistanceX(g0,g0) = 16
    c: DistanceX(g1,g2) = 16
FEATURE [PartDesign::Pocket] Pocket003
  BaseFeature = -> Pocket002
  Length = 5
  Length2 = 100
  Profile = -> Sketch006
  Type = 1
FEATURE [Sketcher::SketchObject] Sketch007
  ExternalGeometry = -> [Pocket003]
  FullyConstrained = true
  MapMode = 5
  Placement = pos=(88,0,0) rot=(0.57735,0.57735,0.57735;2.0944rad)
  Support = -> [Pocket003]
  sketch-geometry (1):
    g0: Circle CenterX=-50 CenterY=56 CenterZ=0 NormalX=0 NormalY=0 NormalZ=1 AngleXU=0 Radius=5
  constraints (2):
    c: Coincident(g0,g-3)
    c: Diameter(g0) = 10
FEATURE [PartDesign::Pad] Pad003
  BaseFeature = -> Pocket003
  Direction = (1,1,1)
  Length = 15
  Length2 = 100
  Profile = -> Sketch007
  Type = 0
FEATURE [Sketcher::SketchObject] Sketch008
  ExternalGeometry = -> [Pad003]
  FullyConstrained = true
  MapMode = 5
  Placement = pos=(-88,0,0) rot=(0.57735,-0.57735,-0.57735;2.0944rad)
  Support = -> [Pad003]
  sketch-geometry (1):
    g0: Circle CenterX=50 CenterY=56 CenterZ=0 NormalX=0 NormalY=0 NormalZ=1 AngleXU=0 Radius=5.25
  constraints (2):
    c: Coincident(g0,g-3)
    c: Diameter(g0) = 10.5
FEATURE [PartDesign::Pad] Pad004
  BaseFeature = -> Pad003
  Direction = (1,1,1)
  Length = 15
  Length2 = 100
  Profile = -> Sketch008
  Type = 0
FEATURE [PartDesign::CoordinateSystem] LCS_axis
  AttacherType = Attacher::AttachEngine3D
  MapMode = 11
  Placement = pos=(88,-50,56) rot=(0.707107,0,0.707107;3.14159rad)
  Support = -> [Pad004]
FEATURE [Sketcher::SketchObject] Sketch009
  ExternalGeometry = -> [Pad004]
  FullyConstrained = true
  MapMode = 5
  Placement = pos=(88,0,0) rot=(0.57735,0.57735,0.57735;2.0944rad)
  Support = -> [Pad004]
  sketch-geometry (6):
    g0: LineSegment StartX=150 StartY=40 StartZ=0 EndX=150 EndY=72 EndZ=0
    g1: LineSegment StartX=150 StartY=72 StartZ=0 EndX=118 EndY=72 EndZ=0
    g2: LineSegment StartX=146 StartY=68 StartZ=0 EndX=122 EndY=68 EndZ=0
    g3: LineSegment StartX=146 StartY=68 StartZ=0 EndX=146 EndY=44 EndZ=0
    g4: ArcOfCircle CenterX=122 CenterY=72 CenterZ=0 NormalX=0 NormalY=0 NormalZ=1 AngleXU=0 Radius=4 StartAngle=3.14159 EndAngle=4.71239
    g5: ArcOfCircle CenterX=150 CenterY=44 CenterZ=0 NormalX=0 NormalY=0 NormalZ=1 AngleXU=0 Radius=4 StartAngle=3.14159 EndAngle=4.71239
  constraints (18):
    c: Coincident(g0,g-3)
    c: Coincident(g0,g-3)
    c: Coincident(g1,g0)
    c: Horizontal(g1)
    c: Horizontal(g2)
    c: Coincident(g3,g2)
    c: Vertical(g3)
    c: Equal(g0,g1)
    c: Equal(g2,g3)
    c: DistanceX(g2,g2) = 24
    c: DistanceY(g2,g0) = 4
    c: DistanceX(g2,g0) = 4
    c: PointOnObject(g4,g1)
    c: Coincident(g4,g2)
    c: Coincident(g4,g1)
    c: PointOnObject(g5,g0)
    c: Coincident(g5,g3)
    c: Coincident(g5,g0)
FEATURE [PartDesign::Pad] Pad005
  BaseFeature = -> Pad004
  Direction = (1,1,1)
  Length = 176
  Length2 = 100
  Profile = -> Sketch009
  Reversed = true
  Type = 0
FEATURE [PartDesign::Body] Body
  Group = -> [Sketch,Pad,Sketch001,Pad001,Sketch002,Pocket,LCS_hole1,LCS_hole2,LCS_1,LCS_front1,LCS_front2,Sketch003,Pad002,Sketch004,Pocket001,Sketch005,Pocket002,Sketch006,Pocket003,Sketch007,Pad003,Sketch008,Pad004,LCS_axis,Sketch009,Pad005]
  Origin = -> Origin
  Tip = -> Pad005
---- part motor.FCStd = doc fcstd_661c0a022bda ----
FCSTD DOCUMENT  (FreeCAD 0.19R)
Label: motor
License: All rights reserved
LicenseURL: http://en.wikipedia.org/wiki/All_rights_reserved
objects: Sketcher::SketchObject×6, PartDesign::Pad×6, PartDesign::Fillet×4, PartDesign::CoordinateSystem×3, PartDesign::Body×1
note: 30 computed .brp shape members not serialized (recipe doc carries the construction recipe); baked Part::Feature solids carry a one-line shape summary decoded from their .brp

FEATURE [Sketcher::SketchObject] Sketch
  FullyConstrained = true
  MapMode = 5
  Placement = pos=(0,0,0) rot=(1,0,0;1.5708rad)
  Support = -> [XZ_Plane]
  sketch-geometry (1):
    g0: Circle CenterX=0 CenterY=0 CenterZ=0 NormalX=0 NormalY=0 NormalZ=1 AngleXU=0 Radius=42.5
  constraints (2):
    c: Coincident(g0,g-1)
    c: Diameter(g0) = 85
FEATURE [PartDesign::Pad] Pad
  Direction = (1,1,1)
  Length = 90
  Length2 = 100
  Placement = pos=(0,0,0) rot=(1,0,0;1.5708rad)
  Profile = -> Sketch
  Type = 0
FEATURE [PartDesign::Fillet] Fillet
  Base = -> Pad [Edge3]
  BaseFeature = -> Pad
  Placement = pos=(0,0,0) rot=(1,0,0;1.5708rad)
  Radius = 5
  SupportTransform = false
FEATURE [PartDesign::Fillet] Fillet001
  Base = -> Fillet [Edge3]
  BaseFeature = -> Fillet
  Placement = pos=(0,0,0) rot=(1,0,0;1.5708rad)
  Radius = 5
  SupportTransform = false
FEATURE [Sketcher::SketchObject] Sketch001
  FullyConstrained = true
  MapMode = 5
  Placement = pos=(0,-90,1.98e-14) rot=(1,0,0;1.5708rad)
  Support = -> [Fillet001]
  sketch-geometry (1):
    g0: Circle CenterX=0 CenterY=0 CenterZ=0 NormalX=0 NormalY=0 NormalZ=1 AngleXU=0 Radius=16.5
  constraints (2):
    c: Coincident(g0,g-1)
    c: Diameter(g0) = 33
FEATURE [PartDesign::Pad] Pad001
  BaseFeature = -> Fillet001
  Direction = (1,1,1)
  Length = 8
  Length2 = 100
  Placement = pos=(0,0,0) rot=(1,0,0;1.5708rad)
  Profile = -> Sketch001
  Type = 0
FEATURE [PartDesign::Fillet] Fillet002
  Base = -> Pad001 [Edge10]
  BaseFeature = -> Pad001
  Placement = pos=(0,0,0) rot=(1,0,0;1.5708rad)
  Radius = 3
  SupportTransform = false
FEATURE [Sketcher::SketchObject] Sketch002
  FullyConstrained = true
  MapMode = 5
  Placement = pos=(0,-98,9.7e-14) rot=(1,0,0;1.5708rad)
  Support = -> [Fillet002]
  sketch-geometry (1):
    g0: Circle CenterX=0 CenterY=0 CenterZ=0 NormalX=0 NormalY=0 NormalZ=1 AngleXU=0 Radius=4
  constraints (2):
    c: Coincident(g0,g-1)
    c: Diameter(g0) = 8
FEATURE [PartDesign::Pad] Pad002
  BaseFeature = -> Fillet002
  Direction = (1,1,1)
  Length = 32
  Length2 = 100
  Placement = pos=(0,0,0) rot=(1,0,0;1.5708rad)
  Profile = -> Sketch002
  Type = 0
FEATURE [Sketcher::SketchObject] Sketch003
  FullyConstrained = true
  MapMode = 5
  Placement = pos=(0,0,0) rot=(-1,0,0;1.5708rad)
  Support = -> [Pad002]
  sketch-geometry (4):
    g0: LineSegment StartX=-20.9225 StartY=21.5 StartZ=0 EndX=20.9225 EndY=21.5 EndZ=0
    g1: LineSegment StartX=-20.9225 StartY=-21.5 StartZ=0 EndX=20.9225 EndY=-21.5 EndZ=0
    g2: ArcOfCircle CenterX=0 CenterY=0 CenterZ=0 NormalX=0 NormalY=0 NormalZ=1 AngleXU=0 Radius=30 StartAngle=5.48417 EndAngle=7.0822
    g3: ArcOfCircle CenterX=0 CenterY=-3.1e-15 CenterZ=0 NormalX=0 NormalY=0 NormalZ=1 AngleXU=0 Radius=30 StartAngle=2.34258 EndAngle=3.9406
  constraints (11):
    c: Horizontal(g0)
    c: Symmetric(g1,g0,g-1)
    c: Symmetric(g1,g1,g-2)
    c: DistanceY(g1,g0) = 43
    c: Coincident(g2,g1)
    c: Coincident(g2,g0)
    c: Coincident(g3,g1)
    c: Coincident(g3,g0)
    c: Coincident(g2,g-1)
    c: Coincident(g3,g2)
    c: Radius(g2) = 30
FEATURE [PartDesign::Pad] Pad003
  BaseFeature = -> Pad002
  Direction = (1,1,1)
  Length = 6
  Length2 = 100
  Placement = pos=(0,0,0) rot=(1,0,0;1.5708rad)
  Profile = -> Sketch003
  Type = 0
FEATURE [Sketcher::SketchObject] Sketch004
  FullyConstrained = true
  MapMode = 5
  Placement = pos=(0,6,-8e-15) rot=(-1,0,0;1.5708rad)
  Support = -> [Pad003]
  sketch-geometry (1):
    g0: Circle CenterX=0 CenterY=0 CenterZ=0 NormalX=0 NormalY=0 NormalZ=1 AngleXU=0 Radius=16.5
  constraints (2):
    c: Coincident(g0,g-1)
    c: Diameter(g0) = 33
FEATURE [PartDesign::Pad] Pad004
  BaseFeature = -> Pad003
  Direction = (1,1,1)
  Length = 10
  Length2 = 100
  Placement = pos=(0,0,0) rot=(1,0,0;1.5708rad)
  Profile = -> Sketch004
  Type = 0
FEATURE [PartDesign::Fillet] Fillet003
  Base = -> Pad004 [Edge30]
  BaseFeature = -> Pad004
  Placement = pos=(0,0,0) rot=(1,0,0;1.5708rad)
  Radius = 3
  SupportTransform = false
FEATURE [Sketcher::SketchObject] Sketch005
  FullyConstrained = true
  MapMode = 5
  Placement = pos=(0,-90,1.98e-14) rot=(1,0,0;1.5708rad)
  Support = -> [Fillet003]
  sketch-geometry (2):
    g0: Circle CenterX=-35 CenterY=0 CenterZ=0 NormalX=0 NormalY=0 NormalZ=1 AngleXU=0 Radius=2.5
    g1: Circle CenterX=35 CenterY=0 CenterZ=0 NormalX=0 NormalY=0 NormalZ=1 AngleXU=0 Radius=2.5
  constraints (5):
    c: PointOnObject(g0,g-1)
    c: DistanceX(g0,g1) = 70
    c: Symmetric(g0,g1,g-2)
    c: Equal(g1,g0)
    c: Diameter(g1) = 5
FEATURE [PartDesign::Pad] Pad005
  BaseFeature = -> Fillet003
  Direction = (1,1,1)
  Length = 11
  Length2 = 100
  Placement = pos=(0,0,0) rot=(1,0,0;1.5708rad)
  Profile = -> Sketch005
  Type = 0
FEATURE [PartDesign::CoordinateSystem] LCS_f1
  AttacherType = Attacher::AttachEngine3D
  MapMode = 11
  Placement = pos=(-35,-90,2.2e-13) rot=(0.57735,-0.57735,0.57735;2.0944rad)
  Support = -> [Pad005]
FEATURE [PartDesign::CoordinateSystem] LCS_f2
  AttacherType = Attacher::AttachEngine3D
  MapMode = 11
  Placement = pos=(35,-90,2.2e-13) rot=(0.57735,-0.57735,0.57735;2.0944rad)
  Support = -> [Pad005]
FEATURE [PartDesign::CoordinateSystem] shaft
  AttacherType = Attacher::AttachEngine3D
  MapMode = 11
  Placement = pos=(0,-130,1.93e-13) rot=(0.57735,-0.57735,0.57735;2.0944rad)
  Support = -> [Pad005]
FEATURE [PartDesign::Body] Body
  Group = -> [Sketch,Pad,Fillet,Fillet001,Sketch001,Pad001,Fillet002,Sketch002,Pad002,Sketch003,Pad003,Sketch004,Pad004,Fillet003,Sketch005,Pad005,LCS_f1,LCS_f2,shaft]
  Origin = -> Origin
  Tip = -> Pad005
---- part stand.FCStd = doc fcstd_fcc337bc9760 ----
FCSTD DOCUMENT  (FreeCAD 0.19R)
Label: stand
License: All rights reserved
LicenseURL: http://en.wikipedia.org/wiki/All_rights_reserved
objects: Sketcher::SketchObject×5, PartDesign::Pad×3, PartDesign::CoordinateSystem×3, PartDesign::Pocket×2, PartDesign::Body×1
note: 19 computed .brp shape members not serialized (recipe doc carries the construction recipe); baked Part::Feature solids carry a one-line shape summary decoded from their .brp

FEATURE [Sketcher::SketchObject] Sketch
  FullyConstrained = true
  MapMode = 5
  Placement = pos=(0,0,0) rot=(1,0,0;1.5708rad)
  Support = -> [XZ_Plane]
  sketch-geometry (8):
    g0: LineSegment StartX=-120 StartY=1.55e-14 StartZ=0 EndX=-120 EndY=32 EndZ=0
    g1: LineSegment StartX=-120 StartY=32 StartZ=0 EndX=120 EndY=32 EndZ=0
    g2: LineSegment StartX=120 StartY=32 StartZ=0 EndX=120 EndY=1.42e-14 EndZ=0
    g3: LineSegment StartX=-116 StartY=4 StartZ=0 EndX=-116 EndY=28 EndZ=0
    g4: LineSegment StartX=-116 StartY=28 StartZ=0 EndX=116 EndY=28 EndZ=0
    g5: LineSegment StartX=116 StartY=28 StartZ=0 EndX=116 EndY=4 EndZ=0
    g6: ArcOfCircle CenterX=-120 CenterY=4 CenterZ=0 NormalX=0 NormalY=0 NormalZ=1 AngleXU=0 Radius=4 StartAngle=4.71239 EndAngle=6.28319
    g7: ArcOfCircle CenterX=120 CenterY=4 CenterZ=0 NormalX=0 NormalY=0 NormalZ=1 AngleXU=0 Radius=4 StartAngle=3.14159 EndAngle=4.71239
  constraints (25):
    c: PointOnObject(g0,g-1)
    c: Vertical(g0)
    c: Coincident(g1,g0)
    c: Horizontal(g1)
    c: Coincident(g2,g1)
    c: Vertical(g2)
    c: DistanceY(g0,g0) = 32
    c: DistanceX(g1,g1) = 240
    c: Symmetric(g2,g0,g-2)
    c: Vertical(g3)
    c: Coincident(g4,g3)
    c: Horizontal(g4)
    c: Coincident(g5,g4)
    c: Vertical(g5)
    c: DistanceX(g0,g3) = 4
    c: DistanceY(g3,g0) = 4
    c: DistanceX(g5,g2) = 4
    c: DistanceY(g3,g3) = 24
    c: Equal(g3,g5)
    c: PointOnObject(g6,g0)
    c: Coincident(g6,g3)
    c: Coincident(g6,g0)
    c: PointOnObject(g7,g2)
    c: Coincident(g7,g5)
    c: Coincident(g7,g2)
FEATURE [PartDesign::Pad] Pad
  Direction = (1,1,1)
  Length = 400
  Length2 = 100
  Placement = pos=(0,0,0) rot=(1,0,0;1.5708rad)
  Profile = -> Sketch
  Type = 0
FEATURE [Sketcher::SketchObject] Sketch001
  ExternalGeometry = -> [Pad]
  FullyConstrained = true
  MapMode = 5
  Placement = pos=(120,0,0) rot=(0.707107,0,0.707107;3.14159rad)
  Support = -> [Pad]
  sketch-geometry (8):
    g0: LineSegment StartX=32 StartY=400 StartZ=0 EndX=1.776e-13 EndY=400 EndZ=0
    g1: LineSegment StartX=4 StartY=396 StartZ=0 EndX=32 EndY=396 EndZ=0
    g2: LineSegment StartX=0 StartY=-1.3e-15 StartZ=0 EndX=32 EndY=0 EndZ=0
    g3: LineSegment StartX=4 StartY=4 StartZ=0 EndX=32 EndY=4 EndZ=0
    g4: LineSegment StartX=32 StartY=0 StartZ=0 EndX=32 EndY=4 EndZ=0
    g5: ArcOfCircle CenterX=4 CenterY=0 CenterZ=0 NormalX=0 NormalY=0 NormalZ=1 AngleXU=0 Radius=4 StartAngle=1.5708 EndAngle=3.14159
    g6: ArcOfCircle CenterX=4 CenterY=400 CenterZ=0 NormalX=0 NormalY=0 NormalZ=1 AngleXU=0 Radius=4 StartAngle=3.14159 EndAngle=4.71239
    g7: LineSegment StartX=32 StartY=396 StartZ=0 EndX=32 EndY=400 EndZ=0
  constraints (22):
    c: Coincident(g0,g-4)
    c: Coincident(g0,g-4)
    c: Horizontal(g1)
    c: DistanceY(g1,g0) = 4
    c: DistanceX(g1,g1) = 28
    c: Coincident(g2,g-1)
    c: Coincident(g2,g-3)
    c: Horizontal(g3)
    c: DistanceX(g3,g3) = 28
    c: DistanceY(g2,g3) = 4
    c: PointOnObject(g3,g-5)
    c: Coincident(g4,g2)
    c: Coincident(g4,g3)
    c: PointOnObject(g5,g2)
    c: Coincident(g5,g3)
    c: Coincident(g5,g2)
    c: PointOnObject(g1,g-5)
    c: PointOnObject(g6,g0)
    c: Coincident(g6,g1)
    c: Coincident(g6,g0)
    c: Coincident(g7,g1)
    c: Coincident(g7,g0)
FEATURE [PartDesign::Pad] Pad001
  BaseFeature = -> Pad
  Direction = (1,1,1)
  Length = 240
  Length2 = 100
  Placement = pos=(0,0,0) rot=(1,0,0;1.5708rad)
  Profile = -> Sketch001
  Reversed = true
  Type = 0
FEATURE [Sketcher::SketchObject] Sketch002
  ExternalGeometry = -> [Pad001]
  FullyConstrained = true
  MapMode = 5
  Placement = pos=(0,0,32) rot=(0,0,1;3.14159rad)
  Support = -> [Pad001]
  sketch-geometry (4):
    g0: LineSegment StartX=88 StartY=32 StartZ=0 EndX=-88 EndY=32 EndZ=0
    g1: LineSegment StartX=-88 StartY=32 StartZ=0 EndX=-88 EndY=368 EndZ=0
    g2: LineSegment StartX=-88 StartY=368 StartZ=0 EndX=88 EndY=368 EndZ=0
    g3: LineSegment StartX=88 StartY=368 StartZ=0 EndX=88 EndY=32 EndZ=0
  constraints (12):
    c: Coincident(g0,g1)
    c: Coincident(g1,g2)
    c: Coincident(g2,g3)
    c: Coincident(g3,g0)
    c: Horizontal(g0)
    c: Horizontal(g2)
    c: Vertical(g1)
    c: Vertical(g3)
    c: DistanceX(g2,g-4) = 32
    c: DistanceY(g2,g-4) = 32
    c: DistanceX(g-3,g0) = 32
    c: DistanceY(g-3,g0) = 32
FEATURE [PartDesign::Pocket] Pocket
  BaseFeature = -> Pad001
  Length = 5
  Length2 = 100
  Placement = pos=(0,0,0) rot=(1,0,0;1.5708rad)
  Profile = -> Sketch002
  Type = 1
FEATURE [Sketcher::SketchObject] Sketch003
  ExternalGeometry = -> [Pocket]
  FullyConstrained = true
  MapMode = 5
  Placement = pos=(0,0,32) rot=(0,0,1;3.14159rad)
  Support = -> [Pocket]
  sketch-geometry (12):
    g0: LineSegment StartX=88 StartY=216 StartZ=0 EndX=88 EndY=184 EndZ=0
    g1: LineSegment StartX=88 StartY=216 StartZ=0 EndX=120 EndY=216 EndZ=0
    g2: LineSegment StartX=-88 StartY=216 StartZ=0 EndX=-120 EndY=216 EndZ=0
    g3: LineSegment StartX=-88 StartY=216 StartZ=0 EndX=-88 EndY=184 EndZ=0
    g4: LineSegment StartX=-116 StartY=212 StartZ=0 EndX=-92 EndY=212 EndZ=0
    g5: LineSegment StartX=-92 StartY=212 StartZ=0 EndX=-92 EndY=188 EndZ=0
    g6: LineSegment StartX=116 StartY=212 StartZ=0 EndX=92 EndY=212 EndZ=0
    g7: LineSegment StartX=92 StartY=212 StartZ=0 EndX=92 EndY=188 EndZ=0
    g8: ArcOfCircle CenterX=-116 CenterY=216 CenterZ=0 NormalX=0 NormalY=0 NormalZ=1 AngleXU=0 Radius=4 StartAngle=3.14159 EndAngle=4.71239
    g9: ArcOfCircle CenterX=-88 CenterY=188 CenterZ=0 NormalX=0 NormalY=0 NormalZ=1 AngleXU=0 Radius=4 StartAngle=3.14159 EndAngle=4.71239
    g10: ArcOfCircle CenterX=88 CenterY=188 CenterZ=0 NormalX=0 NormalY=0 NormalZ=1 AngleXU=0 Radius=4 StartAngle=4.71239 EndAngle=6.28319
    g11: ArcOfCircle CenterX=116 CenterY=216 CenterZ=0 NormalX=0 NormalY=0 NormalZ=1 AngleXU=0 Radius=4 StartAngle=4.71239 EndAngle=6.28319
  constraints (38):
    c: Vertical(g0)
    c: Coincident(g1,g0)
    c: Horizontal(g1)
    c: Horizontal(g2)
    c: Coincident(g3,g2)
    c: Vertical(g3)
    c: Equal(g3,g0)
    c: Equal(g0,g1)
    c: Equal(g1,g2)
    c: DistanceX(g2,g2) = 32
    c: Symmetric(g2,g0,g-2)
    c: Horizontal(g4)
    c: Coincident(g5,g4)
    c: Vertical(g5)
    c: Horizontal(g6)
    c: Coincident(g7,g6)
    c: Vertical(g7)
    c: Equal(g6,g7)
    c: Equal(g7,g5)
    c: Equal(g5,g4)
    c: DistanceX(g4,g4) = 24
    c: DistanceY(g4,g2) = 4
    c: Symmetric(g4,g6,g-2)
    c: DistanceX(g4,g2) = 4
    c: PointOnObject(g8,g2)
    c: Coincident(g8,g4)
    c: Coincident(g8,g2)
    c: PointOnObject(g9,g3)
    c: Coincident(g9,g5)
    c: Coincident(g9,g3)
    c: PointOnObject(g10,g0)
    c: Coincident(g10,g7)
    c: Coincident(g10,g0)
    c: PointOnObject(g11,g1)
    c: Coincident(g11,g6)
    c: Coincident(g11,g1)
    c: PointOnObject(g2,g-3)
    c: DistanceY(g2,g-4) = 184
FEATURE [PartDesign::Pad] Pad002
  BaseFeature = -> Pocket
  Direction = (1,1,1)
  Length = 220
  Length2 = 100
  Placement = pos=(0,0,0) rot=(1,0,0;1.5708rad)
  Profile = -> Sketch003
  Type = 0
FEATURE [Sketcher::SketchObject] Sketch004
  ExternalGeometry = -> [Pad002]
  FullyConstrained = true
  MapMode = 5
  Placement = pos=(92,0,0) rot=(0.707107,0,0.707107;3.14159rad)
  Support = -> [Pad002]
  sketch-geometry (1):
    g0: Circle CenterX=236 CenterY=200 CenterZ=0 NormalX=0 NormalY=0 NormalZ=1 AngleXU=0 Radius=5.25
  constraints (3):
    c: Diameter(g0) = 10.5
    c: DistanceX(g0,g-3) = 16
    c: DistanceY(g0,g-3) = 16
FEATURE [PartDesign::Pocket] Pocket001
  BaseFeature = -> Pad002
  Length = 5
  Length2 = 100
  Placement = pos=(0,0,0) rot=(1,0,0;1.5708rad)
  Profile = -> Sketch004
  Type = 1
FEATURE [PartDesign::CoordinateSystem] LCS_hole
  AttacherType = Attacher::AttachEngine3D
  MapMode = 11
  Placement = pos=(-88,-200,236) rot=(0.57735,-0.57735,0.57735;4.18879rad)
  Support = -> [Pocket001]
FEATURE [PartDesign::CoordinateSystem] LCS_sh1
  AttacherType = Attacher::AttachEngine3D
  MapMode = 11
  Placement = pos=(92,-200,236) rot=(0.57735,-0.57735,0.57735;4.18879rad)
  Support = -> [Pocket001]
FEATURE [PartDesign::CoordinateSystem] LCS_sh2
  AttacherType = Attacher::AttachEngine3D
  MapMode = 11
  Placement = pos=(-92,-200,236) rot=(0.57735,-0.57735,0.57735;4.18879rad)
  Support = -> [Pocket001]
FEATURE [PartDesign::Body] Body
  Group = -> [Sketch,Pad,Sketch001,Pad001,Sketch002,Pocket,Sketch003,Pad002,Sketch004,Pocket001,LCS_hole,LCS_sh1,LCS_sh2]
  Origin = -> Origin
  Tip = -> Pocket001
